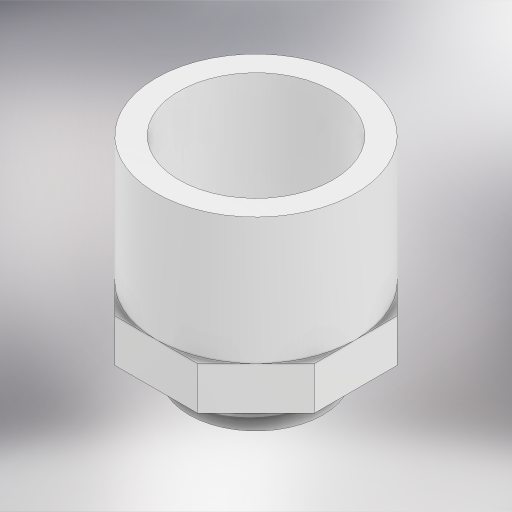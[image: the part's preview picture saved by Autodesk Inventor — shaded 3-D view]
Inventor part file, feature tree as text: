
AUTODESK INVENTOR PART (.ipt)
format: ipt  version: 2023 (Build 270158000, 158)  size: 335,360 bytes
history: native  units: mm
features: extrude x7, sketch x7, other x1, plane x1, thread x1
ambient origin geometry x8: Origin, YZ Plane, XZ Plane, XY Plane, X Axis, Y Axis, Z Axis, Center Point
bodies: Body1 (feature_tree)
feature tree (17):
  other  "Sólido1"
  extrude  "Extrusión1"  Depth=27.76mm
  extrude  "Extrusión2"  Depth=23.6mm
  plane  "Plano de trabajo2"
  extrude  "Extrusión4"  Depth=5.75mm
  extrude  "Extrusión5"  Depth=5.75mm
  extrude  "Extrusión6"  Depth=5.75mm
  extrude  "Extrusión7"  Depth=5.97mm TaperAngle=0.0deg
  thread  "Rosca2"  [1 undecoded]
  extrude  "Extrusión8"  Depth=18.97mm TaperAngle=0.0deg
  sketch  "Boceto1"  dims[d0=21.4mm d1=27.76mm]
  sketch  "Boceto2"  dims[d2=23.6mm d3=0.0mm d5=5.75mm]
  sketch  "Boceto4"  dims[d6=5.75mm d7=5.75mm]
  sketch  "Boceto5"  dims[d8=5.75mm d9=5.75mm]
  sketch  "Boceto6"  dims[d10=5.75mm d11=5.75mm]
  sketch  "Boceto7"  dims[d12=5.75mm d13=5.97mm d14=0.0mm d17=-18.5mm]
  sketch  "Boceto9"  dims[d18=13.6mm d19=18.97mm d20=0.0mm d21=18.97mm d22=0.0mm d25=13.4mm d26=18.6mm d27=18.97mm d28=0.0mm d29=13.6mm d30=18.97mm d31=0.0mm d32=14.87mm d33=0.0mm d34=8.47mm d35=0.0mm]
note: 1 required parameter value undecoded (feature->parameter linkage not recoverable at this tier; creation-order binding heuristic only, values carry confidence <= 0.55)
